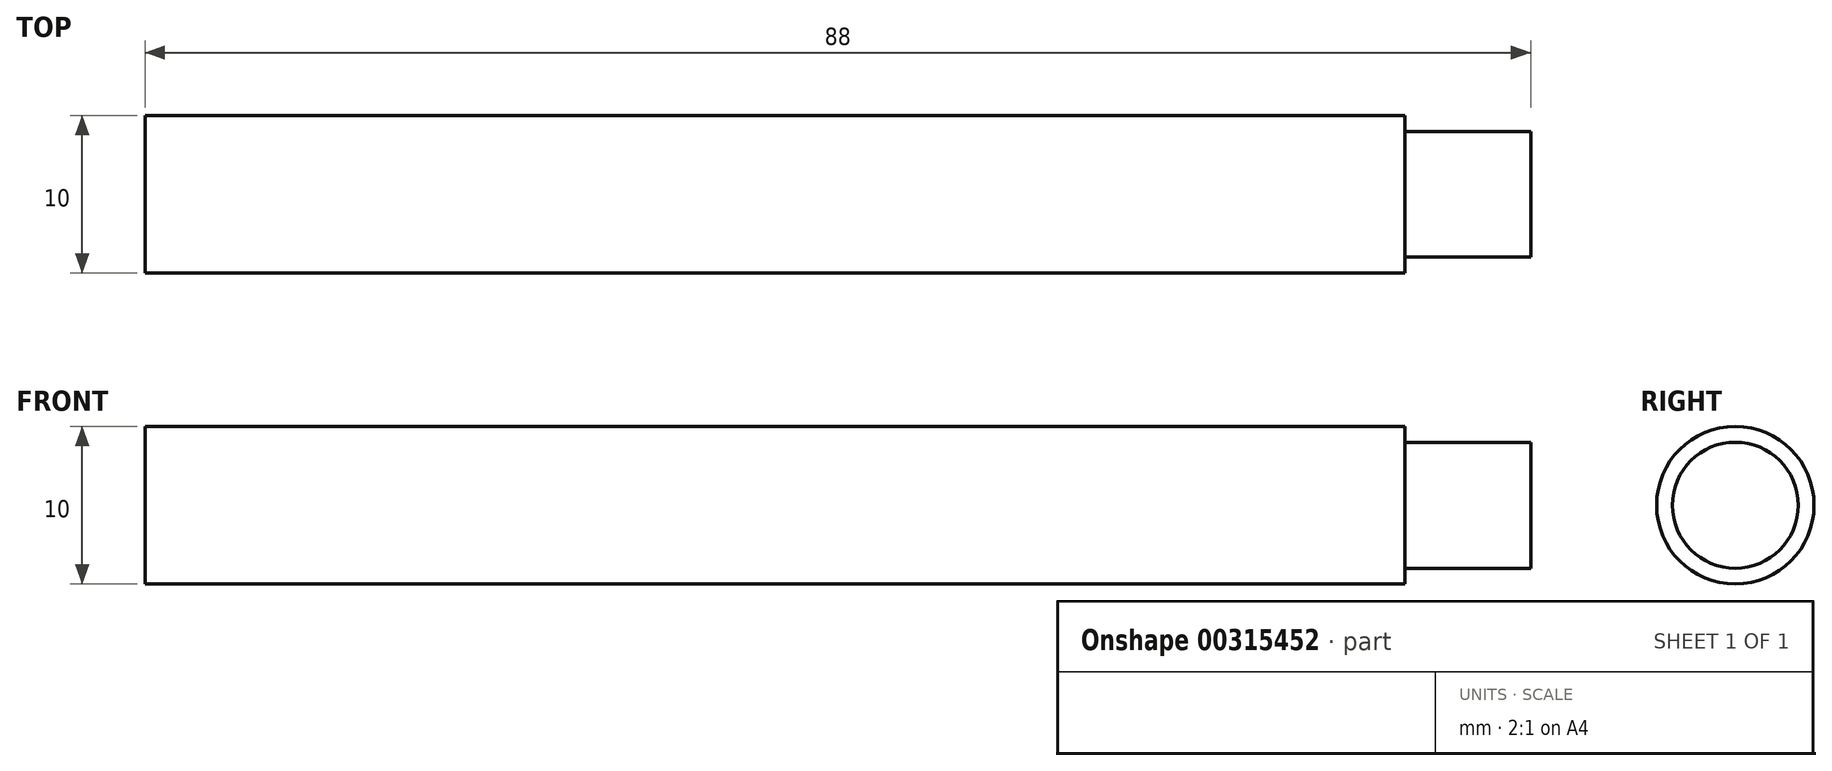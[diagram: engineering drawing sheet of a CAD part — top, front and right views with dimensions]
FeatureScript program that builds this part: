
annotation { "Feature Type Name" : "Feature", "Feature Type Description" : "" }
export const myFeature = defineFeature(function(context is Context, id is Id, definition is map)
    precondition{}
    {
        {
            var Q0;
            Q0=qCreatedBy(makeId("Right.planeOp"),FACE);
            var sketch = newSketch(context, id + "F0", { "sketchPlane" : qUnion([Q0])});
            skCircle(sketch, "E0", {"center": v(0, 0) * mm, "radius": 5 * mm});
            skSolve(sketch);
        }
        {
            var Q0;
            Q0 = qSketchRegion(id + "F0", true);
            extrude(context, id + "F1", {"entities" : qUnion([Q0]), "endBound" : BoundingType.SYMMETRIC, "depth" : 80 * mm});
        }
        {
            var Q0;
            Q0=makeQuery(id+"F1.opExtrude","CAP_FACE",FACE,{"disambiguationData":[OSD([sQuery(id+"F0.wireOp",EDGE,"E0")])],"isStart":false});
            var sketch = newSketch(context, id + "F2", { "sketchPlane" : qUnion([Q0])});
            skCircle(sketch, "E1", {"center": v(0, 0) * mm, "radius": 4 * mm});
            skSolve(sketch);
        }
        {
            var Q0;
            Q0 = qSketchRegion(id + "F2", true);
            extrude(context, id + "F3", {"entities" : qUnion([Q0]), "operationType" : NewBodyOperationType.ADD, "depth" : 8 * mm});
        }
    });
